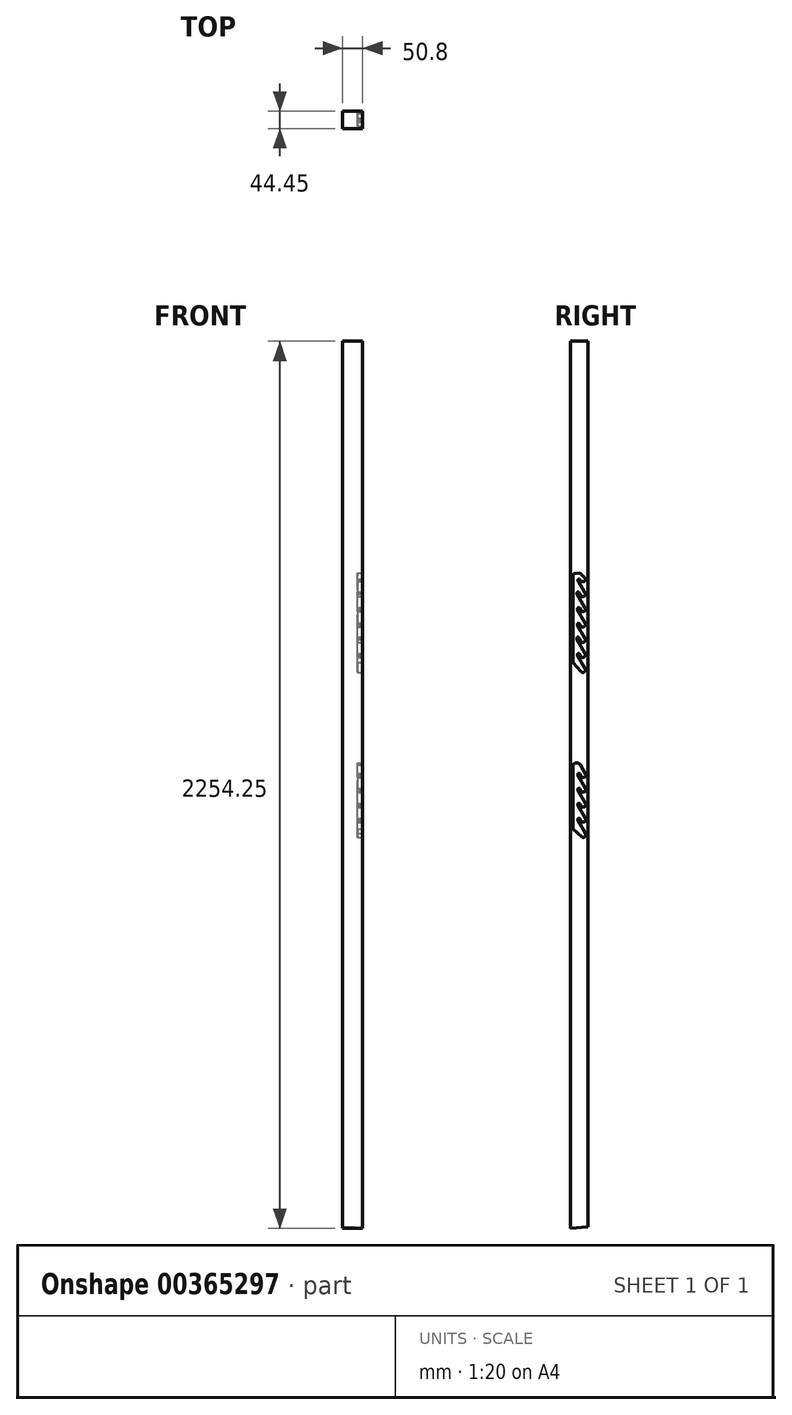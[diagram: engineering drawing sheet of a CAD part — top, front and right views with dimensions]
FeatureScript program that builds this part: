
annotation { "Feature Type Name" : "Feature", "Feature Type Description" : "" }
export const myFeature = defineFeature(function(context is Context, id is Id, definition is map)
    precondition{}
    {
        {
            var Q0;
            Q0=qCreatedBy(makeId("Top.planeOp"),FACE);
            var sketch = newSketch(context, id + "F0", { "sketchPlane" : qUnion([Q0])});
            skLineSegment(sketch, "E0.bottom", {"start": v(0, 0) * mm, "end": v(50.8, 0) * mm});
            skLineSegment(sketch, "E0.top", {"start": v(0, 44.45) * mm, "end": v(50.8, 44.45) * mm});
            skLineSegment(sketch, "E0.left", {"start": v(0, 0) * mm, "end": v(0, 44.45) * mm});
            skLineSegment(sketch, "E0.right", {"start": v(50.8, 0) * mm, "end": v(50.8, 44.45) * mm});
            skSolve(sketch);
        }
        {
            var Q0;
            Q0=makeQuery(id+"F0.imprint","IMPRINT",FACE,{"disambiguationData":[TD([[makeQuery(id+"F0.imprint","IMPRINT",EDGE,{"derivedFrom":sQuery(id+"F0.wireOp",EDGE,"E0.bottom")}),1.0]])]});
            extrude(context, id + "F1", {"entities" : qUnion([Q0]), "depth" : 2254.25 * mm});
        }
        {
            var Q0;
            Q0=makeQuery(id+"F1.opExtrude","SWEPT_FACE",FACE,{"disambiguationData":[OSD([sQuery(id+"F0.wireOp",EDGE,"E0.right")])]});
            var sketch = newSketch(context, id + "F2", { "sketchPlane" : qUnion([Q0])});
            skLineSegment(sketch, "E1", {"start": v(0, 0) * mm, "end": v(44.45, 3.89) * mm});
            skLineSegment(sketch, "E2", {"start": v(44.45, 3.89) * mm, "end": v(44.45, 0) * mm});
            skLineSegment(sketch, "E3", {"start": v(44.45, 0) * mm, "end": v(0, 0) * mm});
            skSolve(sketch);
        }
        {
            var Q0;
            Q0=makeQuery(id+"F2.imprint","IMPRINT",FACE,{"disambiguationData":[TD([[makeQuery(id+"F2.imprint","IMPRINT",EDGE,{"derivedFrom":sQuery(id+"F2.wireOp",EDGE,"E1")}),-1.0]])]});
            extrude(context, id + "F3", {"entities" : qUnion([Q0]), "operationType" : NewBodyOperationType.REMOVE, "oppositeDirection" : true, "depth" : 101.6 * mm});
        }
        {
            var Q0;
            Q0=makeQuery(id+"F3.boolean.opBoolean","COPY",FACE,{"derivedFrom":makeQuery(id+"F3.opExtrude","SWEPT_FACE",FACE,{"disambiguationData":[OSD([sQuery(id+"F2.wireOp",EDGE,"E1")])]})});
            cPlane(context, id + "F4", {"entities" : qUnion([Q0]), "cplaneType" : CPlaneType.OFFSET, "offset" : 746.12 * mm, "oppositeDirection" : true, "width" : 152.4 * mm, "height" : 152.4 * mm});
        }
        {
            var Q0;
            Q0=makeQuery(id+"F3.boolean.opBoolean","COPY",FACE,{"derivedFrom":makeQuery(id+"F3.opExtrude","SWEPT_FACE",FACE,{"disambiguationData":[OSD([sQuery(id+"F2.wireOp",EDGE,"E1")])]})});
            cPlane(context, id + "F5", {"entities" : qUnion([Q0]), "cplaneType" : CPlaneType.OFFSET, "offset" : 1177.92 * mm, "oppositeDirection" : true, "width" : 152.4 * mm, "height" : 152.4 * mm});
        }
        {
            var Q0;
            Q0=makeQuery(id+"F3.boolean.opBoolean","COPY",FACE,{"derivedFrom":makeQuery(id+"F3.opExtrude","SWEPT_FACE",FACE,{"disambiguationData":[OSD([sQuery(id+"F2.wireOp",EDGE,"E1")])]})});
            cPlane(context, id + "F6", {"entities" : qUnion([Q0]), "cplaneType" : CPlaneType.OFFSET, "offset" : 1660.52 * mm, "oppositeDirection" : true, "width" : 152.4 * mm, "height" : 152.4 * mm});
        }
        {
            var Q0;
            Q0=makeQuery(id+"F1.opExtrude","SWEPT_FACE",FACE,{"disambiguationData":[OSD([sQuery(id+"F0.wireOp",EDGE,"E0.right")])]});
            var sketch = newSketch(context, id + "F7", { "sketchPlane" : qUnion([Q0])});
            skLineSegment(sketch, "E4", {"start": v(6.35, 1014.78) * mm, "end": v(6.35, 1150.82) * mm});
            skLineSegment(sketch, "E5.0.3.1", {"start": v(6.35, 1014.78) * mm, "end": v(28.77, 995.3) * mm});
            skArc(sketch, "E5.0.3.2", {"start": v(28.77, 995.3) * mm, "mid": v(36.88, 995.32) * mm, "end": v(37.94, 1003.36) * mm});
            skLineSegment(sketch, "E5.0.3.3", {"start": v(37.94, 1003.36) * mm, "end": v(19.05, 1036.52) * mm});
            skArc(sketch, "E5.0.4.0", {"start": v(23.79, 1041.01) * mm, "mid": v(20.93, 1042.2) * mm, "end": v(19.05, 1039.74) * mm});
            skLineSegment(sketch, "E5.0.4.1", {"start": v(23.79, 1041.01) * mm, "end": v(27.1, 1035.28) * mm});
            skArc(sketch, "E5.0.4.2", {"start": v(27.1, 1035.28) * mm, "mid": v(35.78, 1032.95) * mm, "end": v(38.1, 1041.63) * mm});
            skLineSegment(sketch, "E5.0.4.3", {"start": v(38.1, 1041.63) * mm, "end": v(19.05, 1074.62) * mm});
            skLineSegment(sketch, "E6", {"start": v(19.05, 1036.52) * mm, "end": v(19.05, 1039.74) * mm});
            skArc(sketch, "E7.0.0.5", {"start": v(23.79, 1079.11) * mm, "mid": v(20.93, 1080.3) * mm, "end": v(19.05, 1077.84) * mm});
            skLineSegment(sketch, "E7.4.0.5", {"start": v(23.79, 1079.11) * mm, "end": v(27.1, 1073.38) * mm});
            skArc(sketch, "E7.7.0.5", {"start": v(27.1, 1073.38) * mm, "mid": v(35.78, 1071.05) * mm, "end": v(38.1, 1079.73) * mm});
            skLineSegment(sketch, "E7.11.0.5", {"start": v(38.1, 1079.73) * mm, "end": v(19.05, 1112.72) * mm});
            skArc(sketch, "E8.0.0.6", {"start": v(23.79, 1117.21) * mm, "mid": v(20.93, 1118.4) * mm, "end": v(19.05, 1115.94) * mm});
            skLineSegment(sketch, "E8.4.0.6", {"start": v(23.79, 1117.21) * mm, "end": v(27.1, 1111.48) * mm});
            skArc(sketch, "E8.7.0.6", {"start": v(27.1, 1111.48) * mm, "mid": v(35.78, 1109.15) * mm, "end": v(38.1, 1117.83) * mm});
            skLineSegment(sketch, "E9", {"start": v(19.05, 1074.62) * mm, "end": v(19.05, 1077.84) * mm});
            skLineSegment(sketch, "E10", {"start": v(19.05, 1112.72) * mm, "end": v(19.05, 1115.94) * mm});
            skArc(sketch, "E11.0.0.7", {"start": v(23.79, 1155.31) * mm, "mid": v(20.93, 1156.5) * mm, "end": v(19.05, 1154.04) * mm});
            skLineSegment(sketch, "E11.4.0.7", {"start": v(23.79, 1155.31) * mm, "end": v(27.1, 1149.58) * mm});
            skLineSegment(sketch, "E12", {"start": v(19.05, 1150.82) * mm, "end": v(19.05, 1154.04) * mm});
            skLineSegment(sketch, "E13", {"start": v(6.35, 1150.82) * mm, "end": v(6.35, 1177.13) * mm});
            skLineSegment(sketch, "E14", {"start": v(38.5, 1155.02) * mm, "end": v(25.73, 1177.13) * mm});
            skArc(sketch, "E15", {"start": v(25.73, 1177.13) * mm, "mid": v(16.04, 1182.72) * mm, "end": v(6.35, 1177.13) * mm});
            skLineSegment(sketch, "E16.0.1.1", {"start": v(37.25, 1498.53) * mm, "end": v(18.05, 1531.78) * mm});
            skLineSegment(sketch, "E16.0.1.2", {"start": v(37.25, 1460.43) * mm, "end": v(16.64, 1496.13) * mm});
            skLineSegment(sketch, "E16.0.1.3", {"start": v(37.25, 1422.33) * mm, "end": v(18.31, 1455.12) * mm});
            skLineSegment(sketch, "E16.0.1.7", {"start": v(37.25, 1576.43) * mm, "end": v(17.1, 1611.32) * mm});
            skLineSegment(sketch, "E16.0.1.8", {"start": v(6.35, 1437.87) * mm, "end": v(6.35, 1658.13) * mm});
            skArc(sketch, "E16.0.1.13", {"start": v(27.03, 1414.9) * mm, "mid": v(35.48, 1414.01) * mm, "end": v(37.25, 1422.33) * mm});
            skArc(sketch, "E16.0.1.16", {"start": v(26.25, 1454.08) * mm, "mid": v(34.93, 1451.75) * mm, "end": v(37.25, 1460.43) * mm});
            skArc(sketch, "E16.0.1.18", {"start": v(26.25, 1492.18) * mm, "mid": v(34.93, 1489.85) * mm, "end": v(37.25, 1498.53) * mm});
            skLineSegment(sketch, "E16.0.1.21", {"start": v(18.19, 1571.34) * mm, "end": v(18.2, 1574.51) * mm});
            skArc(sketch, "E16.0.1.23", {"start": v(25.46, 1531.65) * mm, "mid": v(34.71, 1529.17) * mm, "end": v(37.2, 1538.43) * mm});
            skArc(sketch, "E16.0.1.24", {"start": v(26.25, 1608.18) * mm, "mid": v(34.92, 1605.85) * mm, "end": v(37.25, 1614.53) * mm});
            skArc(sketch, "E16.0.1.25", {"start": v(22.95, 1575.8) * mm, "mid": v(20.09, 1576.98) * mm, "end": v(18.2, 1574.51) * mm});
            skLineSegment(sketch, "E16.0.1.26", {"start": v(17.1, 1611.32) * mm, "end": v(17.1, 1614.5) * mm});
            skLineSegment(sketch, "E16.0.1.28", {"start": v(18.05, 1531.78) * mm, "end": v(18.05, 1534.95) * mm});
            skArc(sketch, "E16.0.1.29", {"start": v(22.96, 1535.97) * mm, "mid": v(20.07, 1537.55) * mm, "end": v(18.05, 1534.95) * mm});
            skArc(sketch, "E16.0.1.30", {"start": v(21.87, 1615.77) * mm, "mid": v(18.99, 1617) * mm, "end": v(17.1, 1614.5) * mm});
            skArc(sketch, "E16.0.1.35", {"start": v(21.64, 1500.16) * mm, "mid": v(18.7, 1502.3) * mm, "end": v(16.64, 1499.3) * mm});
            skArc(sketch, "E16.0.1.37", {"start": v(23.05, 1459.62) * mm, "mid": v(20.17, 1460.8) * mm, "end": v(18.31, 1458.3) * mm});
            skLineSegment(sketch, "E16.0.1.39", {"start": v(18.31, 1455.12) * mm, "end": v(18.31, 1458.3) * mm});
            skLineSegment(sketch, "E16.0.1.40", {"start": v(23.05, 1459.62) * mm, "end": v(26.25, 1454.08) * mm});
            skLineSegment(sketch, "E16.0.1.42", {"start": v(16.64, 1496.13) * mm, "end": v(16.64, 1499.3) * mm});
            skLineSegment(sketch, "E16.0.1.43", {"start": v(21.64, 1500.16) * mm, "end": v(26.25, 1492.18) * mm});
            skLineSegment(sketch, "E17.0.1.0", {"start": v(38.1, 2082.95) * mm, "end": v(19.05, 2115.95) * mm});
            skLineSegment(sketch, "E17.0.1.1", {"start": v(6.35, 1909.68) * mm, "end": v(6.35, 2115.2) * mm});
            skLineSegment(sketch, "E17.0.1.2", {"start": v(38.1, 2044.85) * mm, "end": v(19.05, 2077.85) * mm});
            skLineSegment(sketch, "E17.0.1.3", {"start": v(37.92, 1892.2) * mm, "end": v(19.05, 1925.35) * mm});
            skLineSegment(sketch, "E17.0.1.4", {"start": v(38.1, 1930.45) * mm, "end": v(19.05, 1963.45) * mm});
            skLineSegment(sketch, "E17.0.1.5", {"start": v(38.1, 1968.55) * mm, "end": v(19.05, 2001.55) * mm});
            skLineSegment(sketch, "E17.0.1.6", {"start": v(38.1, 2006.65) * mm, "end": v(19.05, 2039.65) * mm});
            skPoint(sketch, "E17.0.1.7", {"position": v(11.83, 2210.9) * mm});
            skArc(sketch, "E17.0.1.11", {"start": v(27.1, 1962.2) * mm, "mid": v(35.78, 1959.88) * mm, "end": v(38.1, 1968.55) * mm});
            skArc(sketch, "E17.0.1.12", {"start": v(27.1, 2076.45) * mm, "mid": v(35.78, 2074.13) * mm, "end": v(38.1, 2082.8) * mm});
            skLineSegment(sketch, "E17.0.1.13", {"start": v(19.05, 2001.55) * mm, "end": v(19.05, 2004.77) * mm});
            skLineSegment(sketch, "E17.0.1.15", {"start": v(6.35, 2115.2) * mm, "end": v(6.35, 2141.73) * mm});
            skArc(sketch, "E17.0.1.16", {"start": v(27.1, 2000.3) * mm, "mid": v(35.78, 1997.98) * mm, "end": v(38.1, 2006.65) * mm});
            skArc(sketch, "E17.0.1.18", {"start": v(27.1, 1924.1) * mm, "mid": v(35.78, 1921.78) * mm, "end": v(38.1, 1930.45) * mm});
            skLineSegment(sketch, "E17.0.1.20", {"start": v(38.1, 2120.3) * mm, "end": v(25.73, 2141.73) * mm});
            skLineSegment(sketch, "E17.0.1.21", {"start": v(23.79, 2006.04) * mm, "end": v(27.1, 2000.3) * mm});
            skArc(sketch, "E17.0.1.22", {"start": v(23.79, 2006.04) * mm, "mid": v(20.93, 2007.22) * mm, "end": v(19.05, 2004.77) * mm});
            skLineSegment(sketch, "E17.0.1.23", {"start": v(23.79, 1967.94) * mm, "end": v(27.1, 1962.2) * mm});
            skArc(sketch, "E17.0.1.24", {"start": v(23.79, 2120.44) * mm, "mid": v(20.93, 2121.62) * mm, "end": v(19.05, 2119.17) * mm});
            skArc(sketch, "E17.0.1.25", {"start": v(27.99, 1885.07) * mm, "mid": v(36.18, 1884.13) * mm, "end": v(37.92, 1892.2) * mm});
            skLineSegment(sketch, "E17.0.1.26", {"start": v(23.79, 2120.29) * mm, "end": v(27.1, 2114.55) * mm});
            skLineSegment(sketch, "E17.0.1.27", {"start": v(19.05, 2115.95) * mm, "end": v(19.05, 2119.17) * mm});
            skLineSegment(sketch, "E17.0.1.28", {"start": v(19.05, 1963.45) * mm, "end": v(19.05, 1966.67) * mm});
            skArc(sketch, "E17.0.1.29", {"start": v(25.73, 2141.73) * mm, "mid": v(16.04, 2147.32) * mm, "end": v(6.35, 2141.73) * mm});
            skArc(sketch, "E17.0.1.30", {"start": v(23.79, 1967.94) * mm, "mid": v(20.93, 1969.12) * mm, "end": v(19.05, 1966.67) * mm});
            skArc(sketch, "E17.0.1.31", {"start": v(23.79, 2082.34) * mm, "mid": v(20.93, 2083.52) * mm, "end": v(19.05, 2081.07) * mm});
            skLineSegment(sketch, "E17.0.1.32", {"start": v(23.79, 1929.84) * mm, "end": v(27.1, 1924.1) * mm});
            skArc(sketch, "E17.0.1.33", {"start": v(23.79, 2044.14) * mm, "mid": v(20.93, 2045.32) * mm, "end": v(19.05, 2042.87) * mm});
            skArc(sketch, "E17.0.1.34", {"start": v(23.79, 1929.84) * mm, "mid": v(20.93, 1931.02) * mm, "end": v(19.05, 1928.57) * mm});
            skLineSegment(sketch, "E17.0.1.35", {"start": v(23.79, 2082.19) * mm, "end": v(27.1, 2076.45) * mm});
            skLineSegment(sketch, "E17.0.1.36", {"start": v(19.05, 2077.85) * mm, "end": v(19.05, 2081.07) * mm});
            skLineSegment(sketch, "E17.0.1.37", {"start": v(19.05, 2039.65) * mm, "end": v(19.05, 2042.87) * mm});
            skLineSegment(sketch, "E17.0.1.39", {"start": v(19.05, 1925.35) * mm, "end": v(19.05, 1928.57) * mm});
            skLineSegment(sketch, "E17.0.1.42", {"start": v(6.35, 1909.68) * mm, "end": v(27.99, 1885.07) * mm});
            skLineSegment(sketch, "E17.direction2", {"start": v(19.05, 1675.07) * mm, "end": v(19.05, 1852.47) * mm, "construction": true});
            skLineSegment(sketch, "E18", {"start": v(6.35, 1437.87) * mm, "end": v(27.03, 1414.9) * mm});
            skLineSegment(sketch, "E19", {"start": v(19.05, 1154.04) * mm, "end": v(19.05, 1150.82) * mm});
            skLineSegment(sketch, "E20", {"start": v(19.05, 1077.84) * mm, "end": v(19.05, 1074.62) * mm});
            skLineSegment(sketch, "E21", {"start": v(19.05, 1150.82) * mm, "end": v(38.1, 1117.83) * mm});
            skArc(sketch, "E22", {"start": v(27.1, 1149.58) * mm, "mid": v(35.74, 1146.14) * mm, "end": v(38.5, 1155.02) * mm});
            skLineSegment(sketch, "E23", {"start": v(23.79, 2044.14) * mm, "end": v(27.1, 2038.5) * mm});
            skArc(sketch, "E24", {"start": v(27.1, 2038.5) * mm, "mid": v(35.75, 2036.22) * mm, "end": v(38.1, 2044.85) * mm});
            skArc(sketch, "E25", {"start": v(27.1, 2114.55) * mm, "mid": v(35.36, 2112.15) * mm, "end": v(38.1, 2120.3) * mm});
            skArc(sketch, "E26", {"start": v(23.24, 1648.86) * mm, "mid": v(19.9, 1649.31) * mm, "end": v(19.05, 1646.05) * mm});
            skLineSegment(sketch, "E27", {"start": v(23.24, 1648.86) * mm, "end": v(27.33, 1644.9) * mm});
            skLineSegment(sketch, "E28", {"start": v(21.87, 1615.77) * mm, "end": v(26.25, 1608.18) * mm});
            skArc(sketch, "E29", {"start": v(27.33, 1644.9) * mm, "mid": v(36.35, 1645.07) * mm, "end": v(36.09, 1654.09) * mm});
            skLineSegment(sketch, "E30", {"start": v(19.05, 1646.05) * mm, "end": v(37.25, 1614.53) * mm});
            skLineSegment(sketch, "E31", {"start": v(22.95, 1575.8) * mm, "end": v(26.25, 1570.08) * mm});
            skArc(sketch, "E32", {"start": v(26.25, 1570.08) * mm, "mid": v(34.93, 1567.75) * mm, "end": v(37.25, 1576.43) * mm});
            skLineSegment(sketch, "E33", {"start": v(18.19, 1571.34) * mm, "end": v(37.2, 1538.43) * mm});
            skLineSegment(sketch, "E34", {"start": v(22.96, 1535.97) * mm, "end": v(25.46, 1531.65) * mm});
            skLineSegment(sketch, "E35", {"start": v(36.09, 1654.09) * mm, "end": v(23.92, 1665.48) * mm});
            skLineSegment(sketch, "E36", {"start": v(23.92, 1665.48) * mm, "end": v(12.15, 1664.45) * mm});
            skPoint(sketch, "E37.visualSharp", {"position": v(6.35, 1663.95) * mm});
            skArc(sketch, "E37.filletArc", {"start": v(12.15, 1664.45) * mm, "mid": v(8.02, 1662.42) * mm, "end": v(6.35, 1658.13) * mm});
            skSolve(sketch);
        }
        {
            var Q0;
            Q0=qSketchRegion(id+"F7",true);
            extrude(context, id + "F8", {"entities" : qUnion([Q0]), "operationType" : NewBodyOperationType.REMOVE, "oppositeDirection" : true, "depth" : 12.7 * mm});
        }
    });
